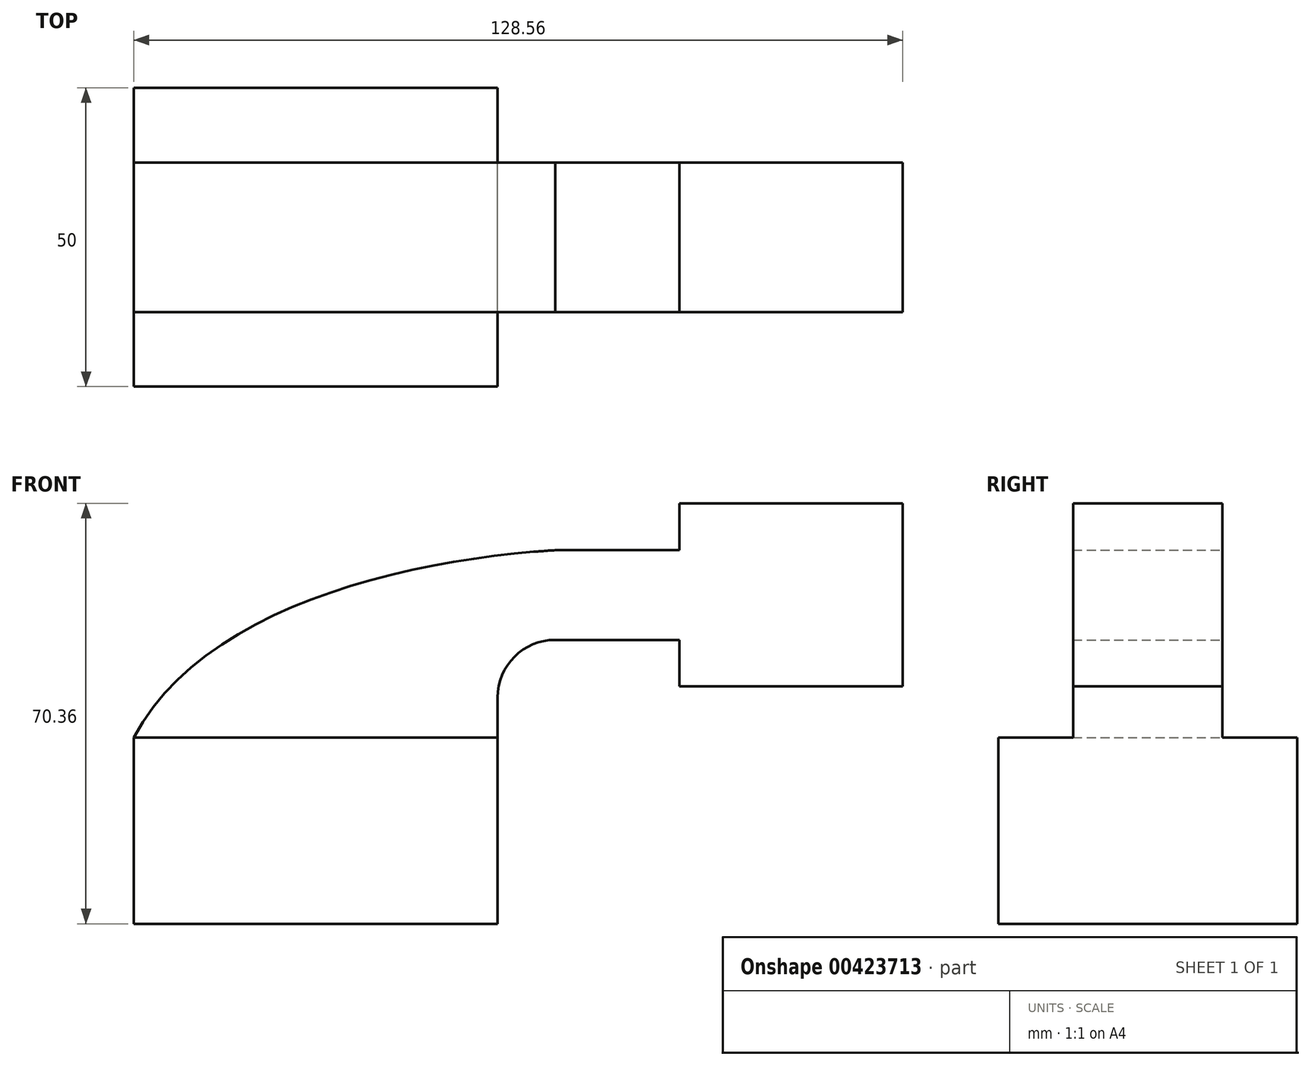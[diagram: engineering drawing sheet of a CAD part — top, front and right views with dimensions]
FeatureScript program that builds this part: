
annotation { "Feature Type Name" : "Feature", "Feature Type Description" : "" }
export const myFeature = defineFeature(function(context is Context, id is Id, definition is map)
    precondition{}
    {
        {
            var Q0;
            Q0=qCreatedBy(makeId("Front.planeOp"),FACE);
            var sketch = newSketch(context, id + "F0", { "sketchPlane" : qUnion([Q0])});
            skLineSegment(sketch, "E0.bottom", {"start": v(0, 0) * mm, "end": v(-60.82, 0) * mm});
            skLineSegment(sketch, "E0.top", {"start": v(0, 31.14) * mm, "end": v(-60.82, 31.14) * mm});
            skLineSegment(sketch, "E0.left", {"start": v(0, 0) * mm, "end": v(0, 31.14) * mm});
            skLineSegment(sketch, "E0.right", {"start": v(-60.82, 0) * mm, "end": v(-60.82, 31.14) * mm});
            skLineSegment(sketch, "E1.bottom", {"start": v(30.4, 70.36) * mm, "end": v(67.74, 70.36) * mm});
            skLineSegment(sketch, "E1.top", {"start": v(30.4, 39.74) * mm, "end": v(67.74, 39.74) * mm});
            skLineSegment(sketch, "E1.left", {"start": v(30.4, 70.36) * mm, "end": v(30.4, 39.74) * mm});
            skLineSegment(sketch, "E1.right", {"start": v(67.74, 70.36) * mm, "end": v(67.74, 39.74) * mm});
            skLineSegment(sketch, "E2", {"start": v(0, 31.14) * mm, "end": v(0, 37.85) * mm});
            skArc(sketch, "E3", {"start": v(0, 37.85) * mm, "mid": v(2.83, 44.68) * mm, "end": v(9.65, 47.5) * mm});
            skLineSegment(sketch, "E4", {"start": v(9.65, 47.5) * mm, "end": v(49.07, 47.5) * mm});
            skLineSegment(sketch, "E5.0", {"start": v(9.65, 62.5) * mm, "end": v(49.07, 62.5) * mm});
            skArc(sketch, "E5.1", {"start": v(-15, 37.85) * mm, "mid": v(-7.78, 55.28) * mm, "end": v(9.65, 62.5) * mm});
            skLineSegment(sketch, "E5.2", {"start": v(-15, 31.14) * mm, "end": v(-15, 37.85) * mm});
            skFitSpline(sketch, "E6", {"points": [v(-60.82, 31.14) * mm, v(9.65, 62.5) * mm], "startDerivative": vector(33.35, 64.8) * mm, "endDerivative": vector(76.13, 4.73) * mm});
            skLineSegment(sketch, "E7", {"start": v(49.07, 70.36) * mm, "end": v(49.07, 39.74) * mm});
            skSolve(sketch);
        }
        {
            var Q0;
            {var subQ3=sQuery(id+"F0.wireOp",EDGE,"E5.2");Q0=makeQuery(id+"F0.imprint","IMPRINT",FACE,{"disambiguationData":[TD([[makeQuery(id+"F0.imprint","IMPRINT",EDGE,{"derivedFrom":subQ3}),1.0]])]});}
            var Q1;
            {var subQ1=sQuery(id+"F0.wireOp",EDGE,"E2");Q1=makeQuery(id+"F0.imprint","IMPRINT",FACE,{"disambiguationData":[TD([[makeQuery(id+"F0.imprint","IMPRINT",EDGE,{"derivedFrom":subQ1}),1.0]])]});}
            extrude(context, id + "F1", {"entities" : qUnion([Q0, Q1]), "endBound" : BoundingType.SYMMETRIC, "depth" : 25 * mm});
        }
        {
            var Q0;
            Q0=makeQuery(id+"F0.imprint","IMPRINT",FACE,{"disambiguationData":[TD([[makeQuery(id+"F0.imprint","IMPRINT",EDGE,{"derivedFrom":sQuery(id+"F0.wireOp",EDGE,"E0.bottom")}),-1.0]])]});
            extrude(context, id + "F2", {"entities" : qUnion([Q0]), "operationType" : NewBodyOperationType.ADD, "endBound" : BoundingType.SYMMETRIC, "depth" : 50 * mm});
        }
        {
            var Q0;
            {var subQ0=sQuery(id+"F0.wireOp",EDGE,"E1.left");var subQ1=sQuery(id+"F0.wireOp",EDGE,"E1.bottom");var subQ2=makeQuery(id+"F0.imprint","INTERSECT",VERTEX,{"derivedFrom":[subQ1,subQ0]});Q0=makeQuery(id+"F0.imprint","IMPRINT",FACE,{"disambiguationData":[TD([[makeQuery(id+"F0.imprint","IMPRINT",EDGE,{"disambiguationData":[TD([[subQ2,-1.0]])],"derivedFrom":subQ1}),-1.0]])]});}
            var Q1;
            {var subQ0=sQuery(id+"F0.wireOp",EDGE,"E5.0");var subQ1=sQuery(id+"F0.wireOp",EDGE,"E1.left");var subQ2=makeQuery(id+"F0.imprint","INTERSECT",VERTEX,{"derivedFrom":[subQ1,subQ0]});Q1=makeQuery(id+"F0.imprint","IMPRINT",FACE,{"disambiguationData":[TD([[makeQuery(id+"F0.imprint","IMPRINT",EDGE,{"disambiguationData":[TD([[subQ2,-1.0]])],"derivedFrom":subQ1}),1.0]])]});}
            var Q2;
            {var subQ0=sQuery(id+"F0.wireOp",EDGE,"E1.left");var subQ1=sQuery(id+"F0.wireOp",EDGE,"E1.top");var subQ2=makeQuery(id+"F0.imprint","INTERSECT",VERTEX,{"derivedFrom":[subQ1,subQ0]});Q2=makeQuery(id+"F0.imprint","IMPRINT",FACE,{"disambiguationData":[TD([[makeQuery(id+"F0.imprint","IMPRINT",EDGE,{"disambiguationData":[TD([[subQ2,-1.0]])],"derivedFrom":subQ1}),1.0]])]});}
            var Q3;
            {var subQ4=sQuery(id+"F0.wireOp",EDGE,"E1.right");Q3=makeQuery(id+"F0.imprint","IMPRINT",FACE,{"disambiguationData":[TD([[makeQuery(id+"F0.imprint","IMPRINT",EDGE,{"derivedFrom":subQ4}),-1.0]])]});}
            extrude(context, id + "F3", {"entities" : qUnion([Q0, Q1, Q2, Q3]), "operationType" : NewBodyOperationType.ADD, "endBound" : BoundingType.SYMMETRIC, "depth" : 25 * mm});
        }
    });
